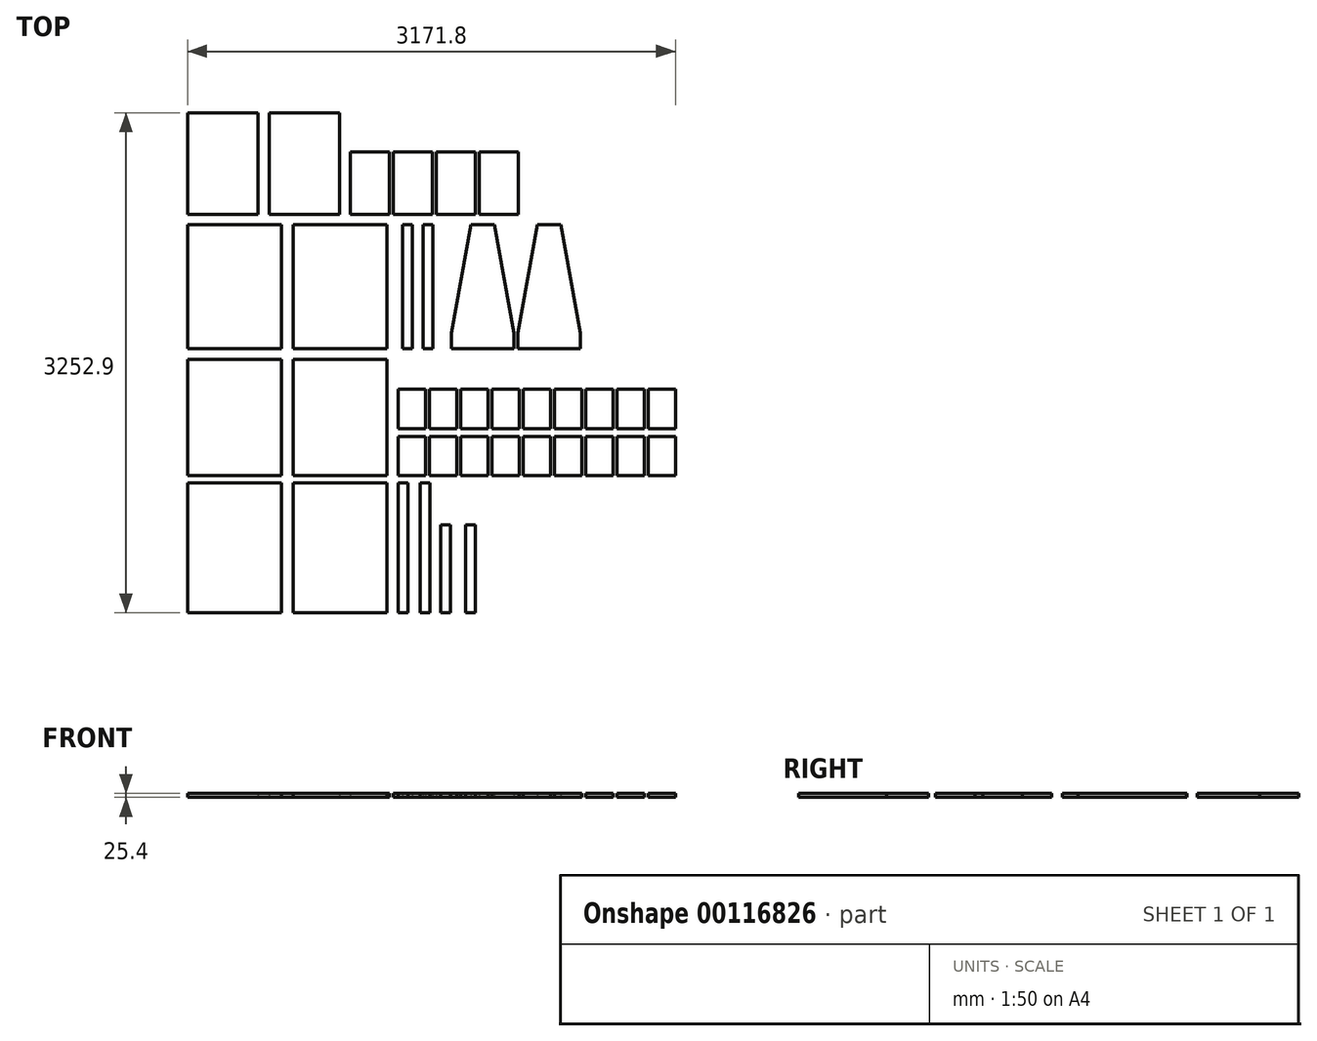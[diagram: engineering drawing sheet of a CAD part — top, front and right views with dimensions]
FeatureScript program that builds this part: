
annotation { "Feature Type Name" : "Feature", "Feature Type Description" : "" }
export const myFeature = defineFeature(function(context is Context, id is Id, definition is map)
    precondition{}
    {
        {
            var Q0;
            Q0=qCreatedBy(makeId("Top.planeOp"),FACE);
            var sketch = newSketch(context, id + "F0", { "sketchPlane" : qUnion([Q0])});
            skLineSegment(sketch, "E0.bottom", {"start": v(0, 0) * mm, "end": v(609.6, 0) * mm});
            skLineSegment(sketch, "E0.top", {"start": v(0, 846.07) * mm, "end": v(609.6, 846.07) * mm});
            skLineSegment(sketch, "E0.left", {"start": v(0, 0) * mm, "end": v(0, 846.07) * mm});
            skLineSegment(sketch, "E0.right", {"start": v(609.6, 0) * mm, "end": v(609.6, 846.07) * mm});
            skLineSegment(sketch, "E1.bottom", {"start": v(685.56, 0) * mm, "end": v(1295.16, 0) * mm});
            skLineSegment(sketch, "E1.top", {"start": v(685.56, 846.07) * mm, "end": v(1295.16, 846.07) * mm});
            skLineSegment(sketch, "E1.left", {"start": v(685.56, 0) * mm, "end": v(685.56, 846.07) * mm});
            skLineSegment(sketch, "E1.right", {"start": v(1295.16, 0) * mm, "end": v(1295.16, 846.07) * mm});
            skLineSegment(sketch, "E2.bottom", {"start": v(0, 891.6) * mm, "end": v(609.6, 891.6) * mm});
            skLineSegment(sketch, "E2.top", {"start": v(0, 1647.25) * mm, "end": v(609.6, 1647.25) * mm});
            skLineSegment(sketch, "E2.left", {"start": v(0, 891.6) * mm, "end": v(0, 1647.25) * mm});
            skLineSegment(sketch, "E2.right", {"start": v(609.6, 891.6) * mm, "end": v(609.6, 1647.25) * mm});
            skLineSegment(sketch, "E3.bottom", {"start": v(685.56, 891.6) * mm, "end": v(1295.16, 891.6) * mm});
            skLineSegment(sketch, "E3.top", {"start": v(685.56, 1647.25) * mm, "end": v(1295.16, 1647.25) * mm});
            skLineSegment(sketch, "E3.left", {"start": v(685.56, 891.6) * mm, "end": v(685.56, 1647.25) * mm});
            skLineSegment(sketch, "E3.right", {"start": v(1295.16, 891.6) * mm, "end": v(1295.16, 1647.25) * mm});
            skLineSegment(sketch, "E4.bottom", {"start": v(0, 1716.6) * mm, "end": v(609.6, 1716.6) * mm});
            skLineSegment(sketch, "E4.top", {"start": v(0, 2524.58) * mm, "end": v(609.6, 2524.58) * mm});
            skLineSegment(sketch, "E4.left", {"start": v(0, 1716.6) * mm, "end": v(0, 2524.58) * mm});
            skLineSegment(sketch, "E4.right", {"start": v(609.6, 1716.6) * mm, "end": v(609.6, 2524.58) * mm});
            skLineSegment(sketch, "E5.bottom", {"start": v(685.56, 1716.6) * mm, "end": v(1295.16, 1716.6) * mm});
            skLineSegment(sketch, "E5.top", {"start": v(685.56, 2524.58) * mm, "end": v(1295.16, 2524.58) * mm});
            skLineSegment(sketch, "E5.left", {"start": v(685.56, 1716.6) * mm, "end": v(685.56, 2524.58) * mm});
            skLineSegment(sketch, "E5.right", {"start": v(1295.16, 1716.6) * mm, "end": v(1295.16, 2524.58) * mm});
            skLineSegment(sketch, "E6.bottom", {"start": v(1397.96, 1716.6) * mm, "end": v(1461.46, 1716.6) * mm});
            skLineSegment(sketch, "E6.top", {"start": v(1397.96, 2524.58) * mm, "end": v(1461.46, 2524.58) * mm});
            skLineSegment(sketch, "E6.left", {"start": v(1397.96, 1716.6) * mm, "end": v(1397.96, 2524.58) * mm});
            skLineSegment(sketch, "E6.right", {"start": v(1461.46, 1716.6) * mm, "end": v(1461.46, 2524.58) * mm});
            skLineSegment(sketch, "E7.bottom", {"start": v(1532.62, 1716.6) * mm, "end": v(1596.12, 1716.6) * mm});
            skLineSegment(sketch, "E7.top", {"start": v(1532.62, 2524.58) * mm, "end": v(1596.12, 2524.58) * mm});
            skLineSegment(sketch, "E7.left", {"start": v(1532.62, 1716.6) * mm, "end": v(1532.62, 2524.58) * mm});
            skLineSegment(sketch, "E7.right", {"start": v(1596.12, 1716.6) * mm, "end": v(1596.12, 2524.58) * mm});
            skLineSegment(sketch, "E8.bottom", {"start": v(1368.4, 0) * mm, "end": v(1431.9, 0) * mm});
            skLineSegment(sketch, "E8.top", {"start": v(1368.4, 846.07) * mm, "end": v(1431.9, 846.07) * mm});
            skLineSegment(sketch, "E8.left", {"start": v(1368.4, 0) * mm, "end": v(1368.4, 846.07) * mm});
            skLineSegment(sketch, "E8.right", {"start": v(1431.9, 0) * mm, "end": v(1431.9, 846.07) * mm});
            skLineSegment(sketch, "E9.bottom", {"start": v(1512.91, 0) * mm, "end": v(1576.41, 0) * mm});
            skLineSegment(sketch, "E9.top", {"start": v(1512.91, 846.07) * mm, "end": v(1576.41, 846.07) * mm});
            skLineSegment(sketch, "E9.left", {"start": v(1512.91, 0) * mm, "end": v(1512.91, 846.07) * mm});
            skLineSegment(sketch, "E9.right", {"start": v(1576.41, 0) * mm, "end": v(1576.41, 846.07) * mm});
            skLineSegment(sketch, "E10.bottom", {"start": v(1644.28, 0) * mm, "end": v(1707.78, 0) * mm});
            skLineSegment(sketch, "E10.top", {"start": v(1644.28, 571.5) * mm, "end": v(1707.78, 571.5) * mm});
            skLineSegment(sketch, "E10.left", {"start": v(1644.28, 0) * mm, "end": v(1644.28, 571.5) * mm});
            skLineSegment(sketch, "E10.right", {"start": v(1707.78, 0) * mm, "end": v(1707.78, 571.5) * mm});
            skLineSegment(sketch, "E11.bottom", {"start": v(1808.5, 0) * mm, "end": v(1872, 0) * mm});
            skLineSegment(sketch, "E11.top", {"start": v(1808.5, 571.5) * mm, "end": v(1872, 571.5) * mm});
            skLineSegment(sketch, "E11.left", {"start": v(1808.5, 0) * mm, "end": v(1808.5, 571.5) * mm});
            skLineSegment(sketch, "E11.right", {"start": v(1872, 0) * mm, "end": v(1872, 571.5) * mm});
            skLineSegment(sketch, "E12.bottom", {"start": v(1368.4, 891.6) * mm, "end": v(1546.2, 891.6) * mm});
            skLineSegment(sketch, "E12.top", {"start": v(1368.4, 1148.14) * mm, "end": v(1546.2, 1148.14) * mm});
            skLineSegment(sketch, "E12.left", {"start": v(1368.4, 891.6) * mm, "end": v(1368.4, 1148.14) * mm});
            skLineSegment(sketch, "E12.right", {"start": v(1546.2, 891.6) * mm, "end": v(1546.2, 1148.14) * mm});
            skLineSegment(sketch, "E13.0.1.0", {"start": v(1546.2, 1198.94) * mm, "end": v(1546.2, 1455.48) * mm});
            skLineSegment(sketch, "E13.0.1.1", {"start": v(1368.4, 1198.94) * mm, "end": v(1546.2, 1198.94) * mm});
            skLineSegment(sketch, "E13.0.1.2", {"start": v(1368.4, 1198.94) * mm, "end": v(1368.4, 1455.48) * mm});
            skLineSegment(sketch, "E13.0.1.3", {"start": v(1368.4, 1455.48) * mm, "end": v(1546.2, 1455.48) * mm});
            skLineSegment(sketch, "E13.1.0.0", {"start": v(1749.4, 891.6) * mm, "end": v(1749.4, 1148.14) * mm});
            skLineSegment(sketch, "E13.1.0.1", {"start": v(1571.6, 891.6) * mm, "end": v(1749.4, 891.6) * mm});
            skLineSegment(sketch, "E13.1.0.2", {"start": v(1571.6, 891.6) * mm, "end": v(1571.6, 1148.14) * mm});
            skLineSegment(sketch, "E13.1.0.3", {"start": v(1571.6, 1148.14) * mm, "end": v(1749.4, 1148.14) * mm});
            skLineSegment(sketch, "E13.1.1.0", {"start": v(1749.4, 1198.94) * mm, "end": v(1749.4, 1455.48) * mm});
            skLineSegment(sketch, "E13.1.1.1", {"start": v(1571.6, 1198.94) * mm, "end": v(1749.4, 1198.94) * mm});
            skLineSegment(sketch, "E13.1.1.2", {"start": v(1571.6, 1198.94) * mm, "end": v(1571.6, 1455.48) * mm});
            skLineSegment(sketch, "E13.1.1.3", {"start": v(1571.6, 1455.48) * mm, "end": v(1749.4, 1455.48) * mm});
            skLineSegment(sketch, "E13.2.0.0", {"start": v(1952.6, 891.6) * mm, "end": v(1952.6, 1148.14) * mm});
            skLineSegment(sketch, "E13.2.0.1", {"start": v(1774.8, 891.6) * mm, "end": v(1952.6, 891.6) * mm});
            skLineSegment(sketch, "E13.2.0.2", {"start": v(1774.8, 891.6) * mm, "end": v(1774.8, 1148.14) * mm});
            skLineSegment(sketch, "E13.2.0.3", {"start": v(1774.8, 1148.14) * mm, "end": v(1952.6, 1148.14) * mm});
            skLineSegment(sketch, "E13.2.1.0", {"start": v(1952.6, 1198.94) * mm, "end": v(1952.6, 1455.48) * mm});
            skLineSegment(sketch, "E13.2.1.1", {"start": v(1774.8, 1198.94) * mm, "end": v(1952.6, 1198.94) * mm});
            skLineSegment(sketch, "E13.2.1.2", {"start": v(1774.8, 1198.94) * mm, "end": v(1774.8, 1455.48) * mm});
            skLineSegment(sketch, "E13.2.1.3", {"start": v(1774.8, 1455.48) * mm, "end": v(1952.6, 1455.48) * mm});
            skLineSegment(sketch, "E13.3.0.0", {"start": v(2155.8, 891.6) * mm, "end": v(2155.8, 1148.14) * mm});
            skLineSegment(sketch, "E13.3.0.1", {"start": v(1978, 891.6) * mm, "end": v(2155.8, 891.6) * mm});
            skLineSegment(sketch, "E13.3.0.2", {"start": v(1978, 891.6) * mm, "end": v(1978, 1148.14) * mm});
            skLineSegment(sketch, "E13.3.0.3", {"start": v(1978, 1148.14) * mm, "end": v(2155.8, 1148.14) * mm});
            skLineSegment(sketch, "E13.3.1.0", {"start": v(2155.8, 1198.94) * mm, "end": v(2155.8, 1455.48) * mm});
            skLineSegment(sketch, "E13.3.1.1", {"start": v(1978, 1198.94) * mm, "end": v(2155.8, 1198.94) * mm});
            skLineSegment(sketch, "E13.3.1.2", {"start": v(1978, 1198.94) * mm, "end": v(1978, 1455.48) * mm});
            skLineSegment(sketch, "E13.3.1.3", {"start": v(1978, 1455.48) * mm, "end": v(2155.8, 1455.48) * mm});
            skLineSegment(sketch, "E13.4.0.0", {"start": v(2359, 891.6) * mm, "end": v(2359, 1148.14) * mm});
            skLineSegment(sketch, "E13.4.0.1", {"start": v(2181.2, 891.6) * mm, "end": v(2359, 891.6) * mm});
            skLineSegment(sketch, "E13.4.0.2", {"start": v(2181.2, 891.6) * mm, "end": v(2181.2, 1148.14) * mm});
            skLineSegment(sketch, "E13.4.0.3", {"start": v(2181.2, 1148.14) * mm, "end": v(2359, 1148.14) * mm});
            skLineSegment(sketch, "E13.4.1.0", {"start": v(2359, 1198.94) * mm, "end": v(2359, 1455.48) * mm});
            skLineSegment(sketch, "E13.4.1.1", {"start": v(2181.2, 1198.94) * mm, "end": v(2359, 1198.94) * mm});
            skLineSegment(sketch, "E13.4.1.2", {"start": v(2181.2, 1198.94) * mm, "end": v(2181.2, 1455.48) * mm});
            skLineSegment(sketch, "E13.4.1.3", {"start": v(2181.2, 1455.48) * mm, "end": v(2359, 1455.48) * mm});
            skLineSegment(sketch, "E13.5.0.0", {"start": v(2562.2, 891.6) * mm, "end": v(2562.2, 1148.14) * mm});
            skLineSegment(sketch, "E13.5.0.1", {"start": v(2384.4, 891.6) * mm, "end": v(2562.2, 891.6) * mm});
            skLineSegment(sketch, "E13.5.0.2", {"start": v(2384.4, 891.6) * mm, "end": v(2384.4, 1148.14) * mm});
            skLineSegment(sketch, "E13.5.0.3", {"start": v(2384.4, 1148.14) * mm, "end": v(2562.2, 1148.14) * mm});
            skLineSegment(sketch, "E13.5.1.0", {"start": v(2562.2, 1198.94) * mm, "end": v(2562.2, 1455.48) * mm});
            skLineSegment(sketch, "E13.5.1.1", {"start": v(2384.4, 1198.94) * mm, "end": v(2562.2, 1198.94) * mm});
            skLineSegment(sketch, "E13.5.1.2", {"start": v(2384.4, 1198.94) * mm, "end": v(2384.4, 1455.48) * mm});
            skLineSegment(sketch, "E13.5.1.3", {"start": v(2384.4, 1455.48) * mm, "end": v(2562.2, 1455.48) * mm});
            skLineSegment(sketch, "E13.6.0.0", {"start": v(2765.4, 891.6) * mm, "end": v(2765.4, 1148.14) * mm});
            skLineSegment(sketch, "E13.6.0.1", {"start": v(2587.6, 891.6) * mm, "end": v(2765.4, 891.6) * mm});
            skLineSegment(sketch, "E13.6.0.2", {"start": v(2587.6, 891.6) * mm, "end": v(2587.6, 1148.14) * mm});
            skLineSegment(sketch, "E13.6.0.3", {"start": v(2587.6, 1148.14) * mm, "end": v(2765.4, 1148.14) * mm});
            skLineSegment(sketch, "E13.6.1.0", {"start": v(2765.4, 1198.94) * mm, "end": v(2765.4, 1455.48) * mm});
            skLineSegment(sketch, "E13.6.1.1", {"start": v(2587.6, 1198.94) * mm, "end": v(2765.4, 1198.94) * mm});
            skLineSegment(sketch, "E13.6.1.2", {"start": v(2587.6, 1198.94) * mm, "end": v(2587.6, 1455.48) * mm});
            skLineSegment(sketch, "E13.6.1.3", {"start": v(2587.6, 1455.48) * mm, "end": v(2765.4, 1455.48) * mm});
            skLineSegment(sketch, "E13.7.0.0", {"start": v(2968.6, 891.6) * mm, "end": v(2968.6, 1148.14) * mm});
            skLineSegment(sketch, "E13.7.0.1", {"start": v(2790.8, 891.6) * mm, "end": v(2968.6, 891.6) * mm});
            skLineSegment(sketch, "E13.7.0.2", {"start": v(2790.8, 891.6) * mm, "end": v(2790.8, 1148.14) * mm});
            skLineSegment(sketch, "E13.7.0.3", {"start": v(2790.8, 1148.14) * mm, "end": v(2968.6, 1148.14) * mm});
            skLineSegment(sketch, "E13.7.1.0", {"start": v(2968.6, 1198.94) * mm, "end": v(2968.6, 1455.48) * mm});
            skLineSegment(sketch, "E13.7.1.1", {"start": v(2790.8, 1198.94) * mm, "end": v(2968.6, 1198.94) * mm});
            skLineSegment(sketch, "E13.7.1.2", {"start": v(2790.8, 1198.94) * mm, "end": v(2790.8, 1455.48) * mm});
            skLineSegment(sketch, "E13.7.1.3", {"start": v(2790.8, 1455.48) * mm, "end": v(2968.6, 1455.48) * mm});
            skLineSegment(sketch, "E13.8.0.0", {"start": v(3171.8, 891.6) * mm, "end": v(3171.8, 1148.14) * mm});
            skLineSegment(sketch, "E13.8.0.1", {"start": v(2994, 891.6) * mm, "end": v(3171.8, 891.6) * mm});
            skLineSegment(sketch, "E13.8.0.2", {"start": v(2994, 891.6) * mm, "end": v(2994, 1148.14) * mm});
            skLineSegment(sketch, "E13.8.0.3", {"start": v(2994, 1148.14) * mm, "end": v(3171.8, 1148.14) * mm});
            skLineSegment(sketch, "E13.8.1.0", {"start": v(3171.8, 1198.94) * mm, "end": v(3171.8, 1455.48) * mm});
            skLineSegment(sketch, "E13.8.1.1", {"start": v(2994, 1198.94) * mm, "end": v(3171.8, 1198.94) * mm});
            skLineSegment(sketch, "E13.8.1.2", {"start": v(2994, 1198.94) * mm, "end": v(2994, 1455.48) * mm});
            skLineSegment(sketch, "E13.8.1.3", {"start": v(2994, 1455.48) * mm, "end": v(3171.8, 1455.48) * mm});
            skLineSegment(sketch, "E13.direction1", {"start": v(1546.2, 891.6) * mm, "end": v(1749.4, 891.6) * mm, "construction": true});
            skLineSegment(sketch, "E13.direction2", {"start": v(1546.2, 891.6) * mm, "end": v(1546.2, 1198.94) * mm, "construction": true});
            skLineSegment(sketch, "E14.bottom", {"start": v(0, 2592.5) * mm, "end": v(457.2, 2592.5) * mm});
            skLineSegment(sketch, "E14.top", {"start": v(0, 3252.9) * mm, "end": v(457.2, 3252.9) * mm});
            skLineSegment(sketch, "E14.left", {"start": v(0, 2592.5) * mm, "end": v(0, 3252.9) * mm});
            skLineSegment(sketch, "E14.right", {"start": v(457.2, 2592.5) * mm, "end": v(457.2, 3252.9) * mm});
            skLineSegment(sketch, "E15.bottom", {"start": v(530.92, 2592.5) * mm, "end": v(988.12, 2592.5) * mm});
            skLineSegment(sketch, "E15.top", {"start": v(530.92, 3252.9) * mm, "end": v(988.12, 3252.9) * mm});
            skLineSegment(sketch, "E15.left", {"start": v(530.92, 2592.5) * mm, "end": v(530.92, 3252.9) * mm});
            skLineSegment(sketch, "E15.right", {"start": v(988.12, 2592.5) * mm, "end": v(988.12, 3252.9) * mm});
            skLineSegment(sketch, "E16.bottom", {"start": v(1059.69, 2592.5) * mm, "end": v(1313.69, 2592.5) * mm});
            skLineSegment(sketch, "E16.top", {"start": v(1059.69, 2998.9) * mm, "end": v(1313.69, 2998.9) * mm});
            skLineSegment(sketch, "E16.left", {"start": v(1059.69, 2592.5) * mm, "end": v(1059.69, 2998.9) * mm});
            skLineSegment(sketch, "E16.right", {"start": v(1313.69, 2592.5) * mm, "end": v(1313.69, 2998.9) * mm});
            skLineSegment(sketch, "E17.1.0.0", {"start": v(1339.09, 2998.9) * mm, "end": v(1593.09, 2998.9) * mm});
            skLineSegment(sketch, "E17.1.0.1", {"start": v(1339.09, 2592.5) * mm, "end": v(1339.09, 2998.9) * mm});
            skLineSegment(sketch, "E17.1.0.2", {"start": v(1593.09, 2592.5) * mm, "end": v(1593.09, 2998.9) * mm});
            skLineSegment(sketch, "E17.1.0.3", {"start": v(1339.09, 2592.5) * mm, "end": v(1593.09, 2592.5) * mm});
            skLineSegment(sketch, "E17.2.0.0", {"start": v(1618.49, 2998.9) * mm, "end": v(1872.49, 2998.9) * mm});
            skLineSegment(sketch, "E17.2.0.1", {"start": v(1618.49, 2592.5) * mm, "end": v(1618.49, 2998.9) * mm});
            skLineSegment(sketch, "E17.2.0.2", {"start": v(1872.49, 2592.5) * mm, "end": v(1872.49, 2998.9) * mm});
            skLineSegment(sketch, "E17.2.0.3", {"start": v(1618.49, 2592.5) * mm, "end": v(1872.49, 2592.5) * mm});
            skLineSegment(sketch, "E17.3.0.0", {"start": v(1897.89, 2998.9) * mm, "end": v(2151.89, 2998.9) * mm});
            skLineSegment(sketch, "E17.3.0.1", {"start": v(1897.89, 2592.5) * mm, "end": v(1897.89, 2998.9) * mm});
            skLineSegment(sketch, "E17.3.0.2", {"start": v(2151.89, 2592.5) * mm, "end": v(2151.89, 2998.9) * mm});
            skLineSegment(sketch, "E17.3.0.3", {"start": v(1897.89, 2592.5) * mm, "end": v(2151.89, 2592.5) * mm});
            skLineSegment(sketch, "E17.direction1", {"start": v(1059.69, 2998.9) * mm, "end": v(1339.09, 2998.9) * mm, "construction": true});
            skLineSegment(sketch, "E18.bottom", {"start": v(1716.53, 1716.6) * mm, "end": v(2122.93, 1716.6) * mm});
            skLineSegment(sketch, "E19", {"start": v(1716.53, 1716.6) * mm, "end": v(1716.53, 1818.2) * mm});
            skLineSegment(sketch, "E20", {"start": v(1716.53, 1818.2) * mm, "end": v(1843.53, 2523.06) * mm});
            skLineSegment(sketch, "E21", {"start": v(1843.53, 2523.06) * mm, "end": v(1995.93, 2523.06) * mm});
            skLineSegment(sketch, "E22", {"start": v(1995.93, 2523.06) * mm, "end": v(2122.93, 1818.2) * mm});
            skLineSegment(sketch, "E23", {"start": v(2122.93, 1818.2) * mm, "end": v(2122.93, 1716.6) * mm});
            skLineSegment(sketch, "E24.1.0.0", {"start": v(2148.33, 1716.6) * mm, "end": v(2148.33, 1818.2) * mm});
            skLineSegment(sketch, "E24.1.0.1", {"start": v(2148.33, 1716.6) * mm, "end": v(2554.73, 1716.6) * mm});
            skLineSegment(sketch, "E24.1.0.2", {"start": v(2554.73, 1818.2) * mm, "end": v(2554.73, 1716.6) * mm});
            skLineSegment(sketch, "E24.1.0.3", {"start": v(2427.73, 2523.06) * mm, "end": v(2554.73, 1818.2) * mm});
            skLineSegment(sketch, "E24.1.0.4", {"start": v(2148.33, 1818.2) * mm, "end": v(2275.33, 2523.06) * mm});
            skLineSegment(sketch, "E24.1.0.5", {"start": v(2275.33, 2523.06) * mm, "end": v(2427.73, 2523.06) * mm});
            skLineSegment(sketch, "E24.direction1", {"start": v(1716.53, 1716.6) * mm, "end": v(2148.33, 1716.6) * mm, "construction": true});
            skSolve(sketch);
        }
        {
            var Q0;
            Q0 = qSketchRegion(id + "F0", true);
            extrude(context, id + "F1", {"entities" : qUnion([Q0]), "depth" : 25.4 * mm});
        }
    });
